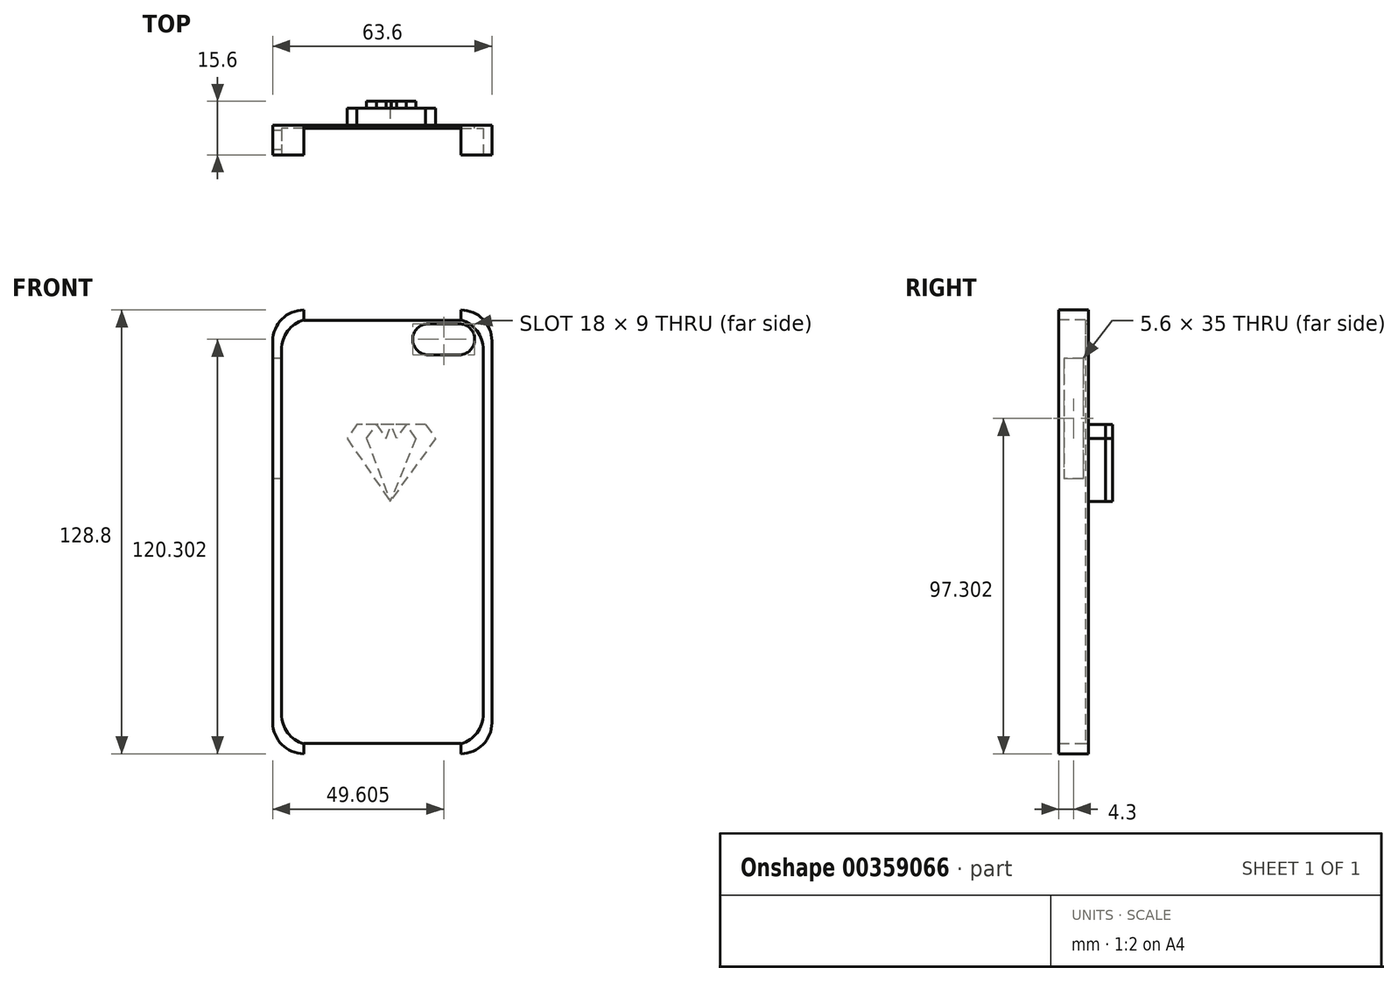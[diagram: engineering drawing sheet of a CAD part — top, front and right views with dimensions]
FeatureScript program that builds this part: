
annotation { "Feature Type Name" : "Feature", "Feature Type Description" : "" }
export const myFeature = defineFeature(function(context is Context, id is Id, definition is map)
    precondition{}
    {
        {
            var Q0;
            Q0=qCreatedBy(makeId("Front.planeOp"),FACE);
            var sketch = newSketch(context, id + "F0", { "sketchPlane" : qUnion([Q0])});
            skLineSegment(sketch, "E0.bottom", {"start": v(-42.12, 64.45) * mm, "end": v(3.48, 64.45) * mm});
            skLineSegment(sketch, "E0.top", {"start": v(-42.12, -64.35) * mm, "end": v(3.48, -64.35) * mm});
            skLineSegment(sketch, "E0.left", {"start": v(-51.12, 55.45) * mm, "end": v(-51.12, -55.35) * mm});
            skLineSegment(sketch, "E0.right", {"start": v(12.48, 55.45) * mm, "end": v(12.48, -55.35) * mm});
            skPoint(sketch, "E1.visualSharp", {"position": v(-51.12, 64.45) * mm});
            skArc(sketch, "E1.filletArc", {"start": v(-42.12, 64.45) * mm, "mid": v(-48.48, 61.82) * mm, "end": v(-51.12, 55.45) * mm});
            skPoint(sketch, "E2.visualSharp", {"position": v(12.48, 64.45) * mm});
            skArc(sketch, "E2.filletArc", {"start": v(12.48, 55.45) * mm, "mid": v(9.85, 61.82) * mm, "end": v(3.48, 64.45) * mm});
            skPoint(sketch, "E3.visualSharp", {"position": v(-51.12, -64.35) * mm});
            skArc(sketch, "E3.filletArc", {"start": v(-51.12, -55.35) * mm, "mid": v(-48.48, -61.71) * mm, "end": v(-42.12, -64.35) * mm});
            skPoint(sketch, "E4.visualSharp", {"position": v(12.48, -64.35) * mm});
            skArc(sketch, "E4.filletArc", {"start": v(3.48, -64.35) * mm, "mid": v(9.85, -61.71) * mm, "end": v(12.48, -55.35) * mm});
            skSolve(sketch);
        }
        {
            var Q0;
            Q0 = qSketchRegion(id + "F0", true);
            extrude(context, id + "F1", {"entities" : qUnion([Q0]), "depth" : 8.6 * mm});
        }
        {
            var Q0;
            Q0=makeQuery(id+"F1.opExtrude","CAP_FACE",FACE,{"disambiguationData":[OSD([sQuery(id+"F0.wireOp",EDGE,"E0.bottom"),sQuery(id+"F0.wireOp",EDGE,"E0.top"),sQuery(id+"F0.wireOp",EDGE,"E0.left"),sQuery(id+"F0.wireOp",EDGE,"E0.right"),sQuery(id+"F0.wireOp",EDGE,"E1.filletArc"),sQuery(id+"F0.wireOp",EDGE,"E2.filletArc"),sQuery(id+"F0.wireOp",EDGE,"E3.filletArc"),sQuery(id+"F0.wireOp",EDGE,"E4.filletArc")])],"isStart":false});
            var sketch = newSketch(context, id + "F2", { "sketchPlane" : qUnion([Q0])});
            skLineSegment(sketch, "E5.bottom", {"start": v(-39.62, 61.95) * mm, "end": v(0.98, 61.95) * mm});
            skLineSegment(sketch, "E5.top", {"start": v(-39.62, -61.85) * mm, "end": v(0.98, -61.85) * mm});
            skLineSegment(sketch, "E5.left", {"start": v(-48.62, 52.95) * mm, "end": v(-48.62, -52.85) * mm});
            skLineSegment(sketch, "E5.right", {"start": v(9.98, 52.95) * mm, "end": v(9.98, -52.85) * mm});
            skPoint(sketch, "E6.visualSharp", {"position": v(-48.62, 61.95) * mm});
            skArc(sketch, "E6.filletArc", {"start": v(-39.62, 61.95) * mm, "mid": v(-45.98, 59.32) * mm, "end": v(-48.62, 52.95) * mm});
            skPoint(sketch, "E7.visualSharp", {"position": v(9.98, 61.95) * mm});
            skArc(sketch, "E7.filletArc", {"start": v(9.98, 52.95) * mm, "mid": v(7.35, 59.32) * mm, "end": v(0.98, 61.95) * mm});
            skPoint(sketch, "E8.visualSharp", {"position": v(9.98, -61.85) * mm});
            skArc(sketch, "E8.filletArc", {"start": v(0.98, -61.85) * mm, "mid": v(7.35, -59.21) * mm, "end": v(9.98, -52.85) * mm});
            skPoint(sketch, "E9.visualSharp", {"position": v(-48.62, -61.85) * mm});
            skArc(sketch, "E9.filletArc", {"start": v(-48.62, -52.85) * mm, "mid": v(-45.98, -59.21) * mm, "end": v(-39.62, -61.85) * mm});
            skSolve(sketch);
        }
        {
            var Q0;
            Q0 = qSketchRegion(id + "F2", true);
            extrude(context, id + "F3", {"entities" : qUnion([Q0]), "operationType" : NewBodyOperationType.REMOVE, "oppositeDirection" : true, "depth" : 7.7 * mm});
        }
        {
            var Q0;
            Q0=makeQuery(id+"F1.opExtrude","CAP_FACE",FACE,{"disambiguationData":[OSD([sQuery(id+"F0.wireOp",EDGE,"E0.bottom"),sQuery(id+"F0.wireOp",EDGE,"E0.top"),sQuery(id+"F0.wireOp",EDGE,"E0.left"),sQuery(id+"F0.wireOp",EDGE,"E0.right"),sQuery(id+"F0.wireOp",EDGE,"E1.filletArc"),sQuery(id+"F0.wireOp",EDGE,"E2.filletArc"),sQuery(id+"F0.wireOp",EDGE,"E3.filletArc"),sQuery(id+"F0.wireOp",EDGE,"E4.filletArc")])],"isStart":true});
            var sketch = newSketch(context, id + "F4", { "sketchPlane" : qUnion([Q0])});
            skLineSegment(sketch, "E10.bottom", {"start": v(-2.98, 60.45) * mm, "end": v(6.02, 60.45) * mm});
            skLineSegment(sketch, "E10.top", {"start": v(-2.98, 51.45) * mm, "end": v(6.02, 51.45) * mm});
            skLineSegment(sketch, "E10.left", {"start": v(-7.48, 55.95) * mm, "end": v(-7.48, 55.95) * mm});
            skLineSegment(sketch, "E10.right", {"start": v(10.52, 55.95) * mm, "end": v(10.52, 55.95) * mm});
            skPoint(sketch, "E11.visualSharp", {"position": v(-7.48, 60.45) * mm});
            skArc(sketch, "E11.filletArc", {"start": v(-2.98, 60.45) * mm, "mid": v(-6.17, 59.13) * mm, "end": v(-7.48, 55.95) * mm});
            skPoint(sketch, "E12.visualSharp", {"position": v(10.52, 60.45) * mm});
            skArc(sketch, "E12.filletArc", {"start": v(10.52, 55.95) * mm, "mid": v(9.2, 59.13) * mm, "end": v(6.02, 60.45) * mm});
            skPoint(sketch, "E13.visualSharp", {"position": v(10.52, 51.45) * mm});
            skArc(sketch, "E13.filletArc", {"start": v(6.02, 51.45) * mm, "mid": v(9.2, 52.77) * mm, "end": v(10.52, 55.95) * mm});
            skPoint(sketch, "E14.visualSharp", {"position": v(-7.48, 51.45) * mm});
            skArc(sketch, "E14.filletArc", {"start": v(-7.48, 55.95) * mm, "mid": v(-6.17, 52.77) * mm, "end": v(-2.98, 51.45) * mm});
            skSolve(sketch);
        }
        {
            var Q0;
            Q0 = qSketchRegion(id + "F4", true);
            extrude(context, id + "F5", {"entities" : qUnion([Q0]), "operationType" : NewBodyOperationType.REMOVE, "oppositeDirection" : true, "depth" : 5 * mm});
        }
        {
            var Q0;
            Q0=makeQuery(id+"F1.opExtrude","SWEPT_FACE",FACE,{"disambiguationData":[OSD([sQuery(id+"F0.wireOp",EDGE,"E0.top")])]});
            var sketch = newSketch(context, id + "F6", { "sketchPlane" : qUnion([Q0])});
            skLineSegment(sketch, "E15.bottom", {"start": v(-42.12, 0) * mm, "end": v(3.48, 0) * mm});
            skLineSegment(sketch, "E15.top", {"start": v(-42.12, 8.6) * mm, "end": v(3.48, 8.6) * mm});
            skLineSegment(sketch, "E15.left", {"start": v(-42.12, 0) * mm, "end": v(-42.12, 8.6) * mm});
            skLineSegment(sketch, "E15.right", {"start": v(3.48, 0) * mm, "end": v(3.48, 8.6) * mm});
            skSolve(sketch);
        }
        {
            var Q0;
            Q0 = qSketchRegion(id + "F6", true);
            extrude(context, id + "F7", {"entities" : qUnion([Q0]), "operationType" : NewBodyOperationType.REMOVE, "oppositeDirection" : true, "depth" : 3 * mm});
        }
        {
            var Q0;
            Q0=makeQuery(id+"F1.opExtrude","SWEPT_FACE",FACE,{"disambiguationData":[OSD([sQuery(id+"F0.wireOp",EDGE,"E0.left")])]});
            var sketch = newSketch(context, id + "F8", { "sketchPlane" : qUnion([Q0])});
            skLineSegment(sketch, "E16.bottom", {"start": v(1.5, 50.45) * mm, "end": v(7.1, 50.45) * mm});
            skLineSegment(sketch, "E16.top", {"start": v(1.5, 15.45) * mm, "end": v(7.1, 15.45) * mm});
            skLineSegment(sketch, "E16.left", {"start": v(1.5, 50.45) * mm, "end": v(1.5, 15.45) * mm});
            skLineSegment(sketch, "E16.right", {"start": v(7.1, 50.45) * mm, "end": v(7.1, 15.45) * mm});
            skSolve(sketch);
        }
        {
            var Q0;
            Q0 = qSketchRegion(id + "F8", true);
            extrude(context, id + "F9", {"entities" : qUnion([Q0]), "operationType" : NewBodyOperationType.REMOVE, "oppositeDirection" : true, "depth" : 14.2 * mm});
        }
        {
            var Q0;
            Q0=makeQuery(id+"F1.opExtrude","SWEPT_FACE",FACE,{"disambiguationData":[OSD([sQuery(id+"F0.wireOp",EDGE,"E0.bottom")])]});
            var sketch = newSketch(context, id + "F10", { "sketchPlane" : qUnion([Q0])});
            skLineSegment(sketch, "E17.bottom", {"start": v(-42.12, -8.6) * mm, "end": v(3.48, -8.6) * mm});
            skLineSegment(sketch, "E17.top", {"start": v(-42.12, 0) * mm, "end": v(3.48, 0) * mm});
            skLineSegment(sketch, "E17.left", {"start": v(-42.12, -8.6) * mm, "end": v(-42.12, 0) * mm});
            skLineSegment(sketch, "E17.right", {"start": v(3.48, -8.6) * mm, "end": v(3.48, 0) * mm});
            skSolve(sketch);
        }
        {
            var Q0;
            Q0 = qSketchRegion(id + "F10", true);
            extrude(context, id + "F11", {"entities" : qUnion([Q0]), "operationType" : NewBodyOperationType.REMOVE, "oppositeDirection" : true, "depth" : 3 * mm});
        }
        {
            var Q0;
            Q0=makeQuery(id+"F1.opExtrude","CAP_FACE",FACE,{"disambiguationData":[OSD([sQuery(id+"F0.wireOp",EDGE,"E0.bottom"),sQuery(id+"F0.wireOp",EDGE,"E0.top"),sQuery(id+"F0.wireOp",EDGE,"E0.left"),sQuery(id+"F0.wireOp",EDGE,"E0.right"),sQuery(id+"F0.wireOp",EDGE,"E1.filletArc"),sQuery(id+"F0.wireOp",EDGE,"E2.filletArc"),sQuery(id+"F0.wireOp",EDGE,"E3.filletArc"),sQuery(id+"F0.wireOp",EDGE,"E4.filletArc")])],"isStart":true});
            var sketch = newSketch(context, id + "F12", { "sketchPlane" : qUnion([Q0])});
            skLineSegment(sketch, "E18", {"start": v(6.75, 31.26) * mm, "end": v(26.75, 31.26) * mm});
            skLineSegment(sketch, "E19", {"start": v(26.75, 31.26) * mm, "end": v(29.58, 27.14) * mm});
            skLineSegment(sketch, "E20", {"start": v(6.75, 31.26) * mm, "end": v(3.92, 27.14) * mm});
            skLineSegment(sketch, "E21", {"start": v(29.58, 27.14) * mm, "end": v(17.06, 8.93) * mm});
            skLineSegment(sketch, "E22", {"start": v(3.92, 27.14) * mm, "end": v(29.58, 27.14) * mm});
            skLineSegment(sketch, "E23", {"start": v(7.86, 27.14) * mm, "end": v(10.69, 31.26) * mm});
            skLineSegment(sketch, "E24", {"start": v(10.69, 31.26) * mm, "end": v(13.52, 27.14) * mm});
            skLineSegment(sketch, "E25", {"start": v(13.52, 27.14) * mm, "end": v(16.35, 31.26) * mm});
            skLineSegment(sketch, "E26", {"start": v(16.35, 31.26) * mm, "end": v(19.2, 27.14) * mm});
            skLineSegment(sketch, "E27", {"start": v(19.2, 27.14) * mm, "end": v(22.04, 31.26) * mm});
            skLineSegment(sketch, "E28", {"start": v(22.04, 31.26) * mm, "end": v(24.9, 27.14) * mm});
            skLineSegment(sketch, "E29", {"start": v(24.9, 27.14) * mm, "end": v(17.06, 8.93) * mm});
            skLineSegment(sketch, "E30", {"start": v(19.2, 27.14) * mm, "end": v(17.06, 8.93) * mm});
            skLineSegment(sketch, "E31", {"start": v(13.52, 27.14) * mm, "end": v(17.06, 8.93) * mm});
            skLineSegment(sketch, "E32", {"start": v(7.86, 27.14) * mm, "end": v(17.06, 8.93) * mm});
            skLineSegment(sketch, "E33", {"start": v(3.92, 27.14) * mm, "end": v(17.06, 8.93) * mm});
            skSolve(sketch);
        }
        {
            var Q0;
            Q0 = qSketchRegion(id + "F12", true);
            extrude(context, id + "F13", {"entities" : qUnion([Q0]), "operationType" : NewBodyOperationType.ADD, "depth" : 5 * mm});
        }
        {
            var Q0;
            Q0=makeQuery(id+"F13.opExtrude","CAP_FACE",FACE,{"disambiguationData":[OSD([sQuery(id+"F12.wireOp",EDGE,"E18"),sQuery(id+"F12.wireOp",EDGE,"E19"),sQuery(id+"F12.wireOp",EDGE,"E20"),sQuery(id+"F12.wireOp",EDGE,"E21"),sQuery(id+"F12.wireOp",EDGE,"E33")])],"isStart":false});
            var sketch = newSketch(context, id + "F14", { "sketchPlane" : qUnion([Q0])});
            skLineSegment(sketch, "E34", {"start": v(3.92, 27.14) * mm, "end": v(29.58, 27.14) * mm});
            skLineSegment(sketch, "E35", {"start": v(6.75, 31.26) * mm, "end": v(9.58, 27.14) * mm});
            skLineSegment(sketch, "E36", {"start": v(26.75, 31.26) * mm, "end": v(23.92, 27.14) * mm});
            skLineSegment(sketch, "E37", {"start": v(9.58, 27.14) * mm, "end": v(12.41, 31.26) * mm});
            skLineSegment(sketch, "E38", {"start": v(23.92, 27.14) * mm, "end": v(21.08, 31.26) * mm});
            skLineSegment(sketch, "E39", {"start": v(21.08, 31.26) * mm, "end": v(18.25, 27.14) * mm});
            skLineSegment(sketch, "E40", {"start": v(12.41, 31.26) * mm, "end": v(15.25, 27.14) * mm});
            skLineSegment(sketch, "E41", {"start": v(15.25, 27.14) * mm, "end": v(16.75, 31.26) * mm});
            skLineSegment(sketch, "E42", {"start": v(18.25, 27.14) * mm, "end": v(16.75, 31.26) * mm});
            skLineSegment(sketch, "E43", {"start": v(9.58, 27.14) * mm, "end": v(17.06, 8.93) * mm});
            skLineSegment(sketch, "E44", {"start": v(15.25, 27.14) * mm, "end": v(17.06, 8.93) * mm});
            skLineSegment(sketch, "E45", {"start": v(18.25, 27.14) * mm, "end": v(17.06, 8.93) * mm});
            skLineSegment(sketch, "E46", {"start": v(23.92, 27.14) * mm, "end": v(17.06, 8.93) * mm});
            skSolve(sketch);
        }
        {
            var Q0;
            Q0 = qSketchRegion(id + "F14", true);
            extrude(context, id + "F15", {"entities" : qUnion([Q0]), "operationType" : NewBodyOperationType.ADD, "depth" : 2 * mm});
        }
    });
